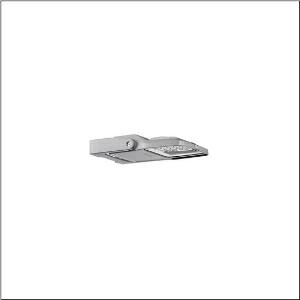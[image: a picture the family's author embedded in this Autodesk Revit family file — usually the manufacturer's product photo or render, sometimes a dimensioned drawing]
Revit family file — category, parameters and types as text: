
# Revit family: floodlight_fl_21_iq_micro___pl64_5xa7761a2e2a_9d46
name_source: partatom
category: Lighting Fixtures
units: mm (PartAtom-declared; Revit-internal decimal feet)

## family parameters
Cut with Voids When Loaded = No
Host = Face
Light Source = No
Part Type = Normal
Room Calculation Point = No
Round Connector Dimension = Use Diameter
Shared = No

## types (1)
- --- (1 x LED, 2870 lm, 23.1 W, 3000K)
    Apparent Load = 23 VA
    CIE Flux Codes = 28 80 98 100 100
    Color Rendering = 70
    Color Temperature = 3000K
    Default Elevation = 1800 mm
    Description = Floodlight FL 21 iQ micro, floodlight, primary light control with lens, of PMMA, primary optical cover: protective disc, of toughened safety glass, transparent, light distribution: PL64, light emission: direct distribution, installation type: surface-mounted, LED, High Power LED, rated luminous flux: 2.870lm, luminous efficacy: 124lm/W, light colour: 730, colour temperature: 3000K, control: optimised constant luminous flux control (CLO 2.0), Desk-Remote (wireless, voltage-free reading and setting of iQ features in the workshop via application-optimized NFC function/RFID function), Light-Fading, Smart-Wire, Night-Set, Lumen-Switch, Temp-Guard, Auto-Match, with terminal, 6-pole, mains connection: 220..240V, AC, 50/60Hz, start of lifetime: 23W, end of service life: 24W, reduction: 11W, luminaire housing, of diecast aluminium, powder-coated, Siteco® metallic grey (DB 702S), corrosivity category C5 mid according to DIN EN ISO 12944, sealing non-destructively replaceable, design bracket, of diecast aluminium, powder-coated, Siteco® metallic grey (DB 702S), protection rating (complete): IP66, insulation class (complete): insulation class II (safety insulation), certification: CE, ENEC, VDE, protection symbol: D, impact resistance: IK07, permissible operating ambient temperature: -40..+40°C, permissible operating ambient temperature for outdoor applications: -40..+50°C, standard: DIN EN 12944, LABS conformity tested according to VDMA 24364:2018-05, packaging unit: 1 piece

Light Distribution: PL64
    Height = 65 mm
    Lamp = 1 x LED
    Lamp Light Flux = 2870 lm
    Lamp Power = 23.1 W
    Lamp count = 1
    Length = 312 mm
    Luminous efficacy = 124 lm/W
    Manufacturer = Siteco
    ModVariant = No
    Model = 5XA7761A2E2A
    Mounting Place = Wall
    Mounting Type = Surface mounted
    Number of Poles = 1
    OnlyDefault = Yes
    Power Factor = 1
    Product Name = Floodlight FL 21 iQ micro | PL64
    Product group = floodlight | wall mounted
    ProductGroupID = 2001
    Protection Class = Protection class II
    Protection Degree = IP 66
    RLX_Detail_Level = 1
    RLX_Emergency_Light_Flux = 0 lm
    RLX_Emergency_Type = 0
    RLX_Emergency_Type_DB = No
    RlxData = <blob elided: 97669 chars, md5=21fef562>
    Socket = socket
    Standby Power = 0 W
    System Light Flux = 2870 lm
    System Power = 23 W
    Type Comments = factory setting: luminous flux: 100 % | dim-lin: 254 | 455 mA
    Type Image = l_1006878.jpg
    URL = http://relux.com
    VarID = @adj_132303
    Voltage = 0 V
    Weight = 0.00 kg
    Width = 230 mm

## geometry (parser evidence)
native form markers: Blend x4, Sweep x13
no freeform markers — native parametric forms only
